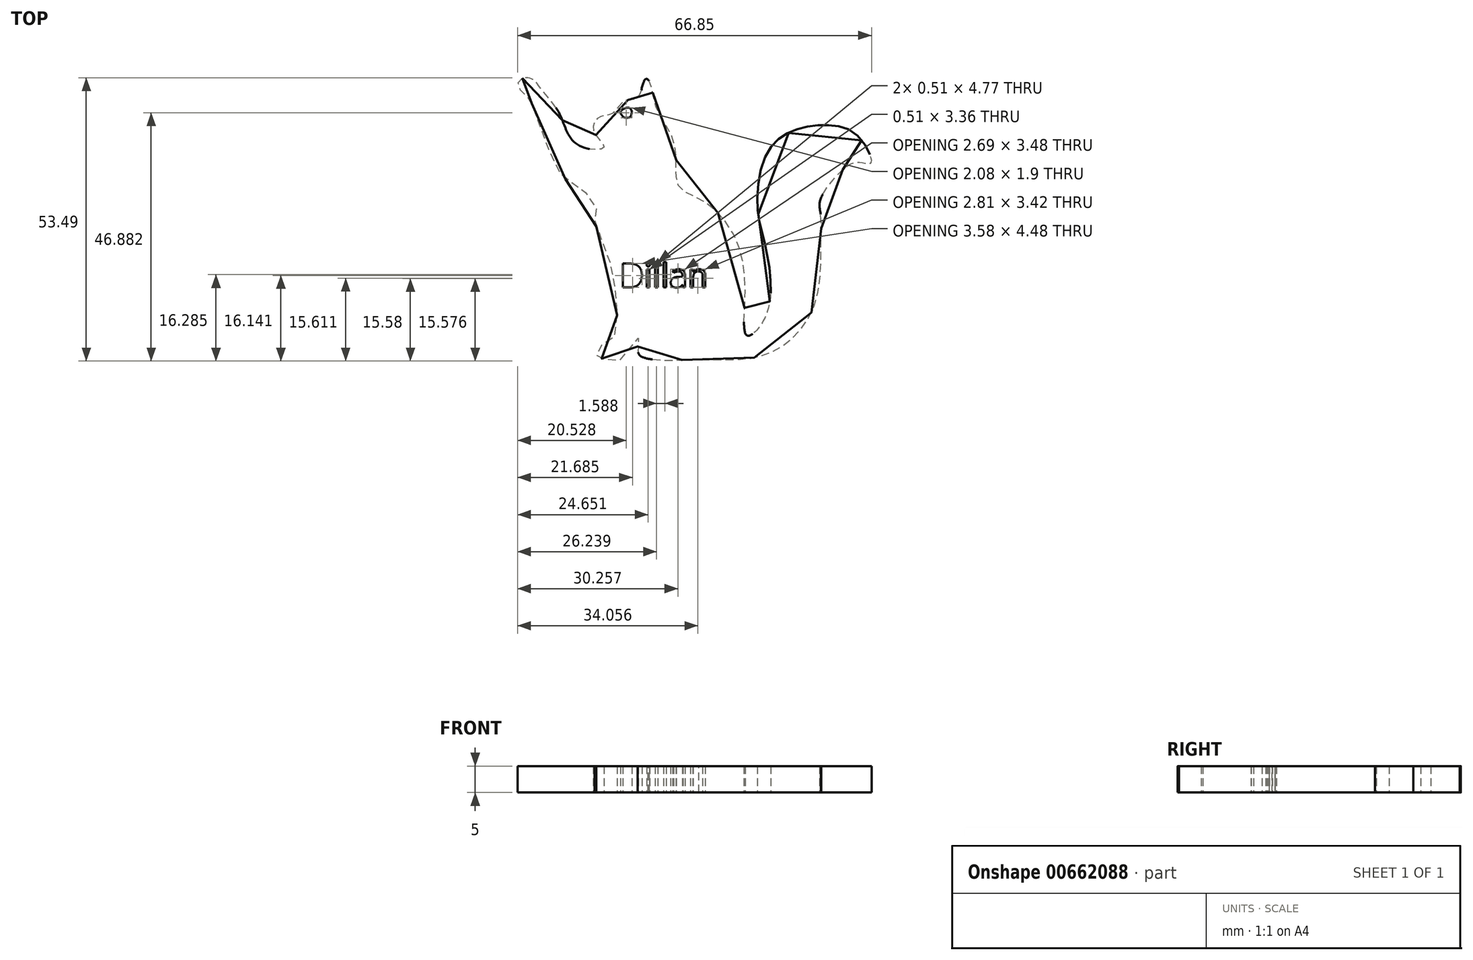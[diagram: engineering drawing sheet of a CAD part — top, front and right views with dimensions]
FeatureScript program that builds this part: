
annotation { "Feature Type Name" : "Feature", "Feature Type Description" : "" }
export const myFeature = defineFeature(function(context is Context, id is Id, definition is map)
    precondition{}
    {
        {
            var Q0;
            Q0=qCreatedBy(makeId("Top.planeOp"),FACE);
            var sketch = newSketch(context, id + "F0", { "sketchPlane" : qUnion([Q0])});
            skPoint(sketch, "E0.11.internal.snap0", {"position": v(-69.28, 29.52) * mm});
            skFitSpline(sketch, "E0", {"points": [v(-68.43, 56.1) * mm, v(-68.82, 55.73) * mm, v(-69.28, 55.17) * mm, v(-69.28, 54.61) * mm, v(-68.66, 53.67) * mm, v(-67.33, 52.38) * mm, v(-66.65, 51.32) * mm, v(-64.95, 46.51) * mm, v(-60.83, 37.5) * mm, v(-58.74, 36.3) * mm, v(-54.57, 31.83) * mm, v(-54.77, 29.52) * mm, v(-52.58, 23.38) * mm, v(-50.8, 14.93) * mm, v(-51.59, 6.5) * mm, v(-54.18, 5.25) * mm, v(-54.26, 3.33) * mm, v(-53.37, 3.1) * mm, v(-49.65, 3) * mm, v(-46.89, 7) * mm, v(-46.56, 7.1) * mm, v(-46.59, 4.35) * mm, v(-45.2, 3.23) * mm, v(-42.4, 2.86) * mm, v(-39.19, 2.86) * mm, v(-34.49, 2.96) * mm, v(-27.83, 2.98) * mm, v(-23.58, 3.6) * mm, v(-18.96, 5.76) * mm, v(-14.41, 10.78) * mm, v(-12.29, 17.76) * mm, v(-12.05, 25.97) * mm, v(-12.1, 30.4) * mm, v(-12.17, 33.12) * mm, v(-8.39, 38.38) * mm, v(-5.44, 40.2) * mm, v(-2.9, 40) * mm, v(-2.48, 40.4) * mm, v(-5.23, 45.34) * mm, v(-11.02, 47.23) * mm, v(-17.29, 46.17) * mm, v(-22.25, 41.91) * mm, v(-24.03, 31.75) * mm, v(-22.6, 24.65) * mm, v(-21.54, 15.55) * mm, v(-23.55, 9.29) * mm, v(-26.03, 7.52) * mm, v(-26.39, 14.73) * mm, v(-27.93, 25.24) * mm, v(-33.95, 32.7) * mm, v(-38.8, 35.53) * mm, v(-39.4, 39.9) * mm, v(-40.22, 45.1) * mm, v(-43.06, 50.3) * mm, v(-44.12, 54.68) * mm, v(-44.94, 55.97) * mm, v(-45.5, 55.44) * mm, v(-46.77, 52.34) * mm, v(-49.08, 51.8) * mm, v(-51.56, 49.38) * mm, v(-53.93, 48.73) * mm, v(-54.93, 46.07) * mm, v(-53.04, 43.06) * mm, v(-58, 43.53) * mm, v(-61.43, 49.38) * mm, v(-64.98, 54.17) * mm, v(-66.63, 55.94) * mm, v(-68.43, 56.1) * mm]});
            skText(sketch, "E1", { "text": "Dillan", "fontName": "OpenSans-Regular.ttf"});
            skFitSpline(sketch, "E2", {"points": [v(-49.3, 50.31) * mm, v(-49.88, 49.75) * mm, v(-49.35, 48.78) * mm, v(-48.06, 48.81) * mm, v(-47.8, 49.92) * mm, v(-48.3, 50.5) * mm, v(-49.3, 50.31) * mm]});
            const initialGuessF0  = {"E1": [-0.05005, 0.0166, 1, 0, 0.00452]};
            skSetInitialGuess(sketch, initialGuessF0);
            skSolve(sketch);
        }
        {
            var Q0;
            Q0 = qSketchRegion(id + "F0", true);
            extrude(context, id + "F1", {"entities" : qUnion([Q0]), "depth" : 5 * mm, "offsetDistance" : 25.4 * mm});
        }
    });
